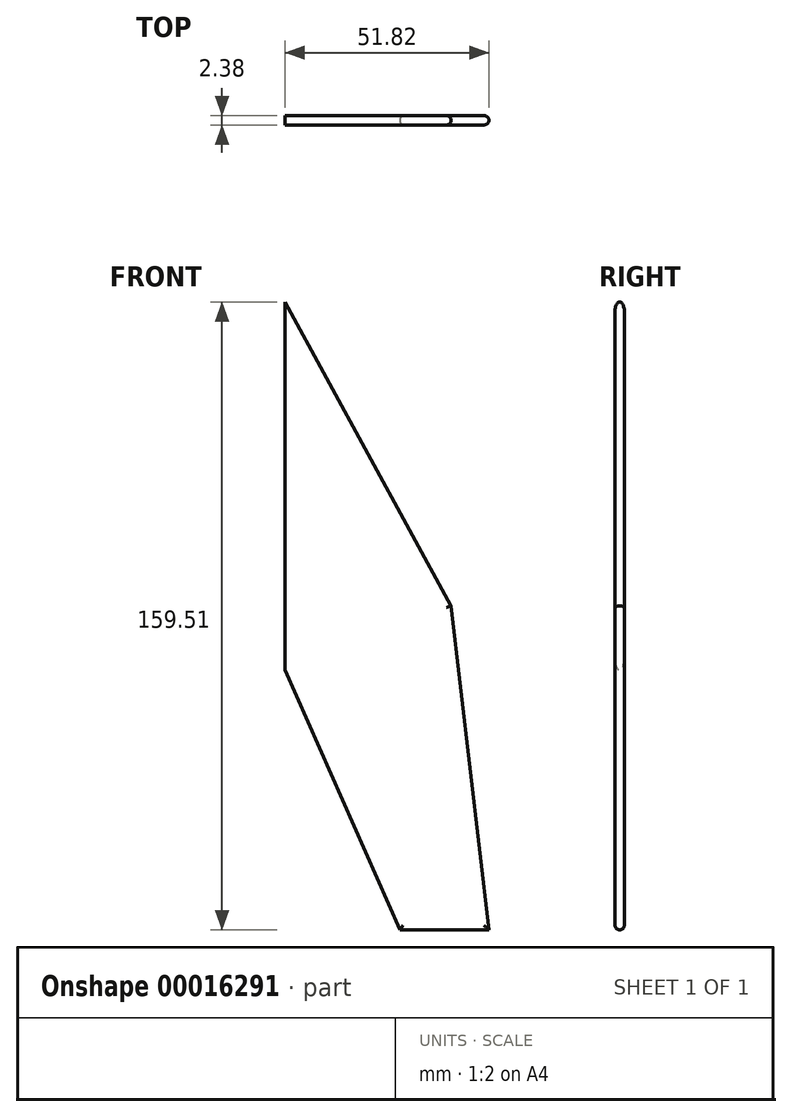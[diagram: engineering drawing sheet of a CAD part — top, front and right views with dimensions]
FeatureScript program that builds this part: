
annotation { "Feature Type Name" : "Feature", "Feature Type Description" : "" }
export const myFeature = defineFeature(function(context is Context, id is Id, definition is map)
    precondition{}
    {
        {
            var Q0;
            Q0=qCreatedBy(makeId("Front.planeOp"),FACE);
            var sketch = newSketch(context, id + "F0", { "sketchPlane" : qUnion([Q0])});
            skLineSegment(sketch, "E0", {"start": v(0, 0) * mm, "end": v(0, -93.47) * mm});
            skLineSegment(sketch, "E1", {"start": v(0, -93.47) * mm, "end": v(29.21, -159.51) * mm});
            skLineSegment(sketch, "E2", {"start": v(29.21, -159.51) * mm, "end": v(51.82, -159.51) * mm});
            skLineSegment(sketch, "E3", {"start": v(51.82, -159.51) * mm, "end": v(42.16, -77.22) * mm});
            skLineSegment(sketch, "E4", {"start": v(42.16, -77.22) * mm, "end": v(0, 0) * mm});
            skSolve(sketch);
        }
        {
            var Q0;
            Q0=makeQuery(id+"F0.imprint","IMPRINT",FACE,{"disambiguationData":[TD([[makeQuery(id+"F0.imprint","IMPRINT",EDGE,{"derivedFrom":sQuery(id+"F0.wireOp",EDGE,"E0")}),1.0]])]});
            extrude(context, id + "F1", {"entities" : qUnion([Q0]), "depth" : 2.38 * mm, "symmetric" : true});
        }
        {
            var Q0;
            Q0=makeQuery(id+"F1.opExtrude","CAP_EDGE",EDGE,{"disambiguationData":[OSD([sQuery(id+"F0.wireOp",EDGE,"E4")])],"isStart":false});
            var Q1;
            Q1=makeQuery(id+"F1.opExtrude","CAP_EDGE",EDGE,{"disambiguationData":[OSD([sQuery(id+"F0.wireOp",EDGE,"E3")])],"isStart":false});
            var Q2;
            Q2=makeQuery(id+"F1.opExtrude","CAP_EDGE",EDGE,{"disambiguationData":[OSD([sQuery(id+"F0.wireOp",EDGE,"E2")])],"isStart":false});
            var Q3;
            Q3=makeQuery(id+"F1.opExtrude","CAP_EDGE",EDGE,{"disambiguationData":[OSD([sQuery(id+"F0.wireOp",EDGE,"E1")])],"isStart":false});
            var Q4;
            Q4=makeQuery(id+"F1.opExtrude","CAP_EDGE",EDGE,{"disambiguationData":[OSD([sQuery(id+"F0.wireOp",EDGE,"E3")])],"isStart":true});
            var Q5;
            Q5=makeQuery(id+"F1.opExtrude","CAP_EDGE",EDGE,{"disambiguationData":[OSD([sQuery(id+"F0.wireOp",EDGE,"E2")])],"isStart":true});
            var Q6;
            Q6=makeQuery(id+"F1.opExtrude","CAP_EDGE",EDGE,{"disambiguationData":[OSD([sQuery(id+"F0.wireOp",EDGE,"E1")])],"isStart":true});
            var Q7;
            Q7=makeQuery(id+"F1.opExtrude","CAP_EDGE",EDGE,{"disambiguationData":[OSD([sQuery(id+"F0.wireOp",EDGE,"E4")])],"isStart":true});
            fillet(context, id + "F2", {"entities" : qUnion([Q0, Q1, Q2, Q3, Q4, Q5, Q6, Q7]), "radius" : 1.2 * mm, "allowEdgeOverflow" : false});
        }
    });
